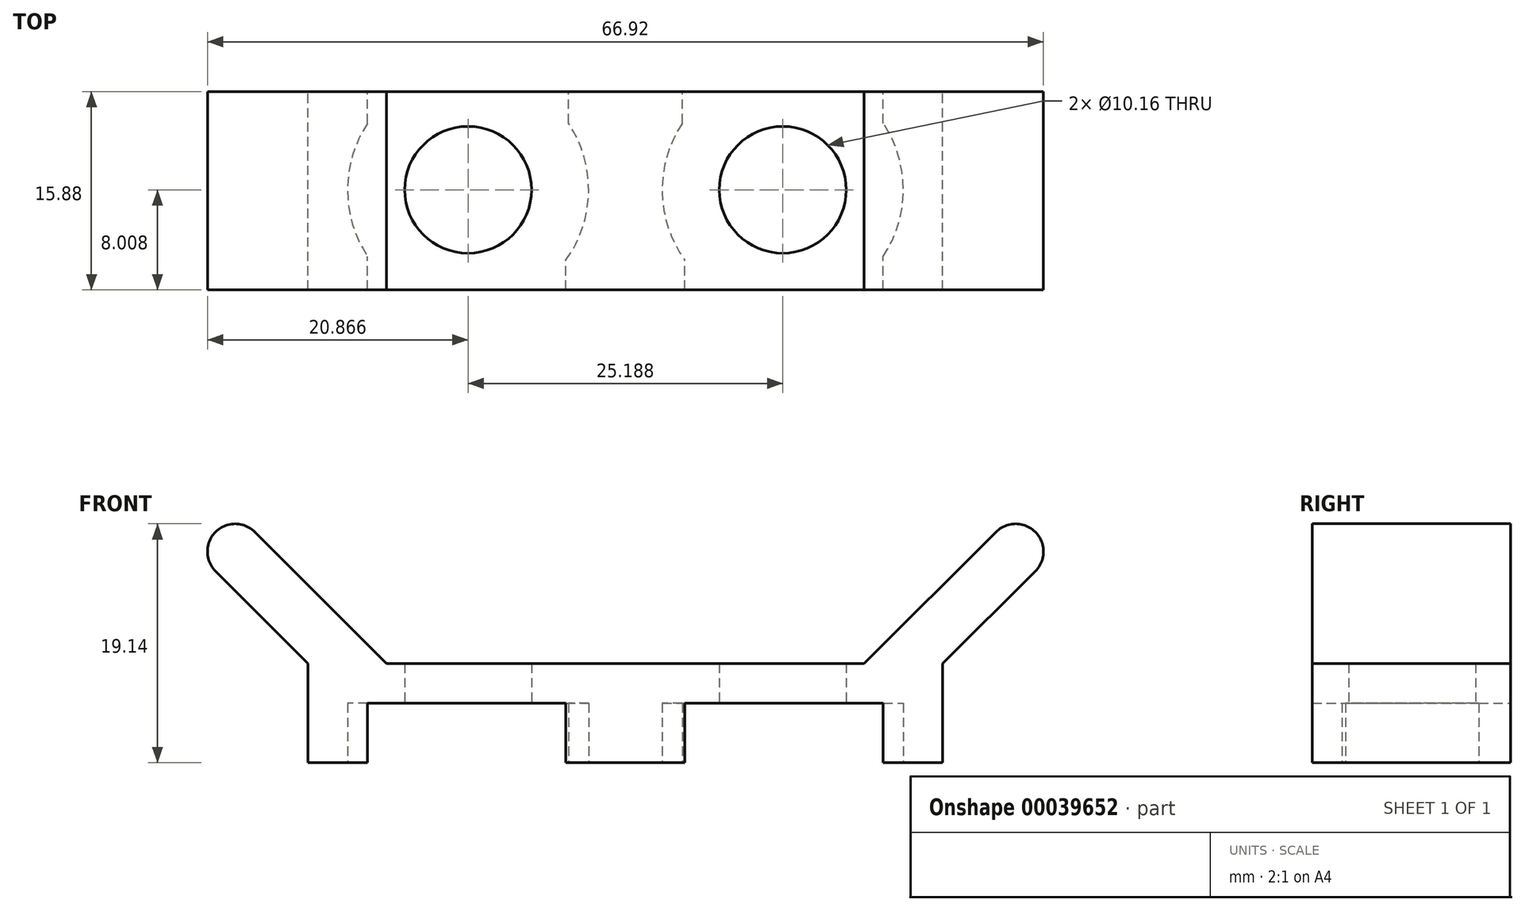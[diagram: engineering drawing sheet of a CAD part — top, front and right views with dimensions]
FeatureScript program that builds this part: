
annotation { "Feature Type Name" : "Feature", "Feature Type Description" : "" }
export const myFeature = defineFeature(function(context is Context, id is Id, definition is map)
    precondition{}
    {
        {
            var Q0;
            Q0=qCreatedBy(makeId("Top.planeOp"),FACE);
            var sketch = newSketch(context, id + "F0", { "sketchPlane" : qUnion([Q0])});
            skLineSegment(sketch, "E0", {"start": v(0, 0) * mm, "end": v(0, 15.88) * mm});
            skLineSegment(sketch, "E1", {"start": v(0, 15.88) * mm, "end": v(25.4, 15.88) * mm});
            skLineSegment(sketch, "E2", {"start": v(25.4, 15.88) * mm, "end": v(25.4, 0) * mm});
            skLineSegment(sketch, "E3", {"start": v(25.4, 0) * mm, "end": v(0, 0) * mm});
            skLineSegment(sketch, "E4", {"start": v(0, 15.88) * mm, "end": v(3.18, 15.88) * mm});
            skPoint(sketch, "E5.endSnap0", {"position": v(3.28, 8) * mm});
            skArc(sketch, "E6", {"start": v(7.21, 15.87) * mm, "mid": v(3.15, 7.88) * mm, "end": v(7.42, 0) * mm});
            skPoint(sketch, "E7.startSnap0", {"position": v(25.4, 7.94) * mm});
            skArc(sketch, "E8.trimOffspring", {"start": v(18.2, 0) * mm, "mid": v(22.46, 7.88) * mm, "end": v(18.4, 15.88) * mm});
            skLineSegment(sketch, "E9", {"start": v(0, 0) * mm, "end": v(4.76, 0) * mm});
            skLineSegment(sketch, "E10", {"start": v(4.76, 0) * mm, "end": v(4.76, 2.67) * mm});
            skLineSegment(sketch, "E11", {"start": v(4.76, 13.34) * mm, "end": v(4.76, 15.88) * mm});
            skLineSegment(sketch, "E12", {"start": v(25.4, 0) * mm, "end": v(20.64, 0) * mm});
            skLineSegment(sketch, "E13", {"start": v(20.64, 0) * mm, "end": v(20.64, 2.37) * mm});
            skLineSegment(sketch, "E14", {"start": v(20.85, 13.34) * mm, "end": v(20.85, 15.88) * mm});
            skLineSegment(sketch, "E15.MirrorCS", {"start": v(50.8, 15.88) * mm, "end": v(25.4, 15.88) * mm});
            skLineSegment(sketch, "E16.MirrorCS", {"start": v(25.4, 0) * mm, "end": v(30.16, 0) * mm});
            skLineSegment(sketch, "E17.MirrorCS", {"start": v(30.16, 0) * mm, "end": v(30.16, 2.37) * mm});
            skLineSegment(sketch, "E18.MirrorCS", {"start": v(29.95, 13.34) * mm, "end": v(29.95, 15.88) * mm});
            skArc(sketch, "E19.MirrorCS", {"start": v(32.6, 0) * mm, "mid": v(28.34, 7.88) * mm, "end": v(32.4, 15.88) * mm});
            skLineSegment(sketch, "E20.MirrorCS", {"start": v(25.4, 0) * mm, "end": v(50.8, 0) * mm});
            skLineSegment(sketch, "E21.MirrorCS", {"start": v(50.8, 0) * mm, "end": v(50.8, 15.88) * mm});
            skArc(sketch, "E22.MirrorCS", {"start": v(43.59, 15.88) * mm, "mid": v(47.65, 7.88) * mm, "end": v(43.38, 0) * mm});
            skLineSegment(sketch, "E23.MirrorCS", {"start": v(46.04, 13.34) * mm, "end": v(46.04, 15.88) * mm});
            skLineSegment(sketch, "E24.MirrorCS", {"start": v(46.04, 0) * mm, "end": v(46.04, 2.67) * mm});
            skSolve(sketch);
        }
        {
            var Q0;
            {var subQ4=sQuery(id+"F0.wireOp",EDGE,"E0");Q0=makeQuery(id+"F0.imprint","IMPRINT",FACE,{"disambiguationData":[TD([[makeQuery(id+"F0.imprint","IMPRINT",EDGE,{"derivedFrom":subQ4}),-1.0]])]});}
            var Q1;
            {var subQ0=sQuery(id+"F0.wireOp",EDGE,"E2");Q1=makeQuery(id+"F0.imprint","IMPRINT",FACE,{"disambiguationData":[TD([[makeQuery(id+"F0.imprint","IMPRINT",EDGE,{"derivedFrom":subQ0}),-1.0]])]});}
            var Q2;
            {var subQ2=sQuery(id+"F0.wireOp",EDGE,"E2");Q2=makeQuery(id+"F0.imprint","IMPRINT",FACE,{"disambiguationData":[TD([[makeQuery(id+"F0.imprint","IMPRINT",EDGE,{"derivedFrom":subQ2}),1.0]])]});}
            var Q3;
            {var subQ3=sQuery(id+"F0.wireOp",EDGE,"E21.MirrorCS");Q3=makeQuery(id+"F0.imprint","IMPRINT",FACE,{"disambiguationData":[TD([[makeQuery(id+"F0.imprint","IMPRINT",EDGE,{"derivedFrom":subQ3}),1.0]])]});}
            extrude(context, id + "F1", {"entities" : qUnion([Q0, Q1, Q2, Q3]), "depth" : 4.76 * mm});
        }
        {
            var Q0;
            Q0=makeQuery(id+"F1.opExtrude","CAP_FACE",FACE,{"disambiguationData":[OSD([sQuery(id+"F0.wireOp",EDGE,"E0"),sQuery(id+"F0.wireOp",EDGE,"E1"),sQuery(id+"F0.wireOp",EDGE,"E4"),sQuery(id+"F0.wireOp",EDGE,"E6"),sQuery(id+"F0.wireOp",EDGE,"E9"),sQuery(id+"F0.wireOp",EDGE,"E10"),sQuery(id+"F0.wireOp",EDGE,"E11")])],"isStart":false});
            var sketch = newSketch(context, id + "F2", { "sketchPlane" : qUnion([Q0])});
            skPoint(sketch, "E25.0", {"position": v(0, 15.88) * mm});
            skPoint(sketch, "E26.0", {"position": v(4.76, 15.88) * mm});
            skPoint(sketch, "E27.0", {"position": v(20.64, 0) * mm});
            skPoint(sketch, "E28.0", {"position": v(0, 0) * mm});
            skLineSegment(sketch, "E29", {"start": v(0, 15.88) * mm, "end": v(4.76, 15.88) * mm});
            skLineSegment(sketch, "E30", {"start": v(20.64, 0) * mm, "end": v(0, 0) * mm});
            skLineSegment(sketch, "E31", {"start": v(0, 15.88) * mm, "end": v(0, 0) * mm});
            skCircle(sketch, "E32", {"center": v(12.8, 8) * mm, "radius": 5.08 * mm});
            skLineSegment(sketch, "E33", {"start": v(20.64, 0) * mm, "end": v(25.4, 0) * mm});
            skLineSegment(sketch, "E34", {"start": v(25.4, 0) * mm, "end": v(25.4, 2.23) * mm});
            skLineSegment(sketch, "E35.MirrorCS", {"start": v(30.16, 0) * mm, "end": v(25.4, 0) * mm});
            skLineSegment(sketch, "E36.MirrorCS", {"start": v(30.16, 0) * mm, "end": v(50.8, 0) * mm});
            skLineSegment(sketch, "E37.MirrorCS", {"start": v(50.8, 15.88) * mm, "end": v(50.8, 0) * mm});
            skLineSegment(sketch, "E38.MirrorCS", {"start": v(50.8, 15.88) * mm, "end": v(46.04, 15.88) * mm});
            skCircle(sketch, "E39.MirrorC", {"center": v(38, 8) * mm, "radius": 5.08 * mm});
            skLineSegment(sketch, "E40", {"start": v(4.76, 15.88) * mm, "end": v(25.4, 15.88) * mm});
            skLineSegment(sketch, "E41", {"start": v(25.4, 15.88) * mm, "end": v(25.4, 0) * mm});
            skLineSegment(sketch, "E42", {"start": v(25.4, 15.88) * mm, "end": v(46.04, 15.88) * mm});
            skSolve(sketch);
        }
        {
            var Q0;
            Q0=makeQuery(id+"F2.imprint","IMPRINT",FACE,{"disambiguationData":[TD([[makeQuery(id+"F2.imprint","IMPRINT",EDGE,{"derivedFrom":sQuery(id+"F2.wireOp",EDGE,"E32")}),-1.0]])]});
            var Q1;
            {var subQ0=sQuery(id+"F2.wireOp",EDGE,"E35.MirrorCS");Q1=makeQuery(id+"F2.imprint","IMPRINT",FACE,{"disambiguationData":[TD([[makeQuery(id+"F2.imprint","IMPRINT",EDGE,{"derivedFrom":subQ0}),-1.0]])]});}
            var Q2;
            Q2=makeQuery(id+"F2.imprint","IMPRINT",FACE,{"disambiguationData":[TD([[makeQuery(id+"F2.imprint","IMPRINT",EDGE,{"derivedFrom":sQuery(id+"F2.wireOp",EDGE,"E29")}),-1.0]])]});
            extrude(context, id + "F3", {"entities" : qUnion([Q0, Q1, Q2]), "depth" : 3.17 * mm});
        }
        {
            var Q0;
            Q0=makeQuery(id+"F1.opExtrude","SWEPT_BODY",BODY,{"disambiguationData":[OSD([sQuery(id+"F0.wireOp",EDGE,"E0"),sQuery(id+"F0.wireOp",EDGE,"E1"),sQuery(id+"F0.wireOp",EDGE,"E4"),sQuery(id+"F0.wireOp",EDGE,"E6"),sQuery(id+"F0.wireOp",EDGE,"E9"),sQuery(id+"F0.wireOp",EDGE,"E10"),sQuery(id+"F0.wireOp",EDGE,"E11")])]});
            var Q1;
            Q1=makeQuery(id+"F3.opExtrude","SWEPT_BODY",BODY,{"disambiguationData":[OSD([sQuery(id+"F2.wireOp",EDGE,"E29"),sQuery(id+"F2.wireOp",EDGE,"E30"),sQuery(id+"F2.wireOp",EDGE,"E31"),sQuery(id+"F2.wireOp",EDGE,"E32"),sQuery(id+"F2.wireOp",EDGE,"E33"),sQuery(id+"F2.wireOp",EDGE,"E35.MirrorCS"),sQuery(id+"F2.wireOp",EDGE,"E36.MirrorCS"),sQuery(id+"F2.wireOp",EDGE,"E37.MirrorCS"),sQuery(id+"F2.wireOp",EDGE,"E38.MirrorCS"),sQuery(id+"F2.wireOp",EDGE,"E39.MirrorC"),sQuery(id+"F2.wireOp",EDGE,"E40"),sQuery(id+"F2.wireOp",EDGE,"E42")])]});
            var Q2;
            Q2=makeQuery(id+"F1.opExtrude","SWEPT_BODY",BODY,{"disambiguationData":[OSD([sQuery(id+"F0.wireOp",EDGE,"E1"),sQuery(id+"F0.wireOp",EDGE,"E8.trimOffspring"),sQuery(id+"F0.wireOp",EDGE,"E12"),sQuery(id+"F0.wireOp",EDGE,"E13"),sQuery(id+"F0.wireOp",EDGE,"E14"),sQuery(id+"F0.wireOp",EDGE,"E15.MirrorCS"),sQuery(id+"F0.wireOp",EDGE,"E17.MirrorCS"),sQuery(id+"F0.wireOp",EDGE,"E18.MirrorCS"),sQuery(id+"F0.wireOp",EDGE,"E19.MirrorCS"),sQuery(id+"F0.wireOp",EDGE,"E20.MirrorCS")])]});
            var Q3;
            Q3=makeQuery(id+"F1.opExtrude","SWEPT_BODY",BODY,{"disambiguationData":[OSD([sQuery(id+"F0.wireOp",EDGE,"E15.MirrorCS"),sQuery(id+"F0.wireOp",EDGE,"E20.MirrorCS"),sQuery(id+"F0.wireOp",EDGE,"E21.MirrorCS"),sQuery(id+"F0.wireOp",EDGE,"E22.MirrorCS"),sQuery(id+"F0.wireOp",EDGE,"E23.MirrorCS"),sQuery(id+"F0.wireOp",EDGE,"E24.MirrorCS")])]});
            booleanBodies(context, id + "F4", {"operationType" : BooleanOperationType.UNION, "tools" : qUnion([Q0, Q1, Q2, Q3])});
        }
        {
            var Q0;
            {var subQ0=sQuery(id+"F0.wireOp",EDGE,"E20.MirrorCS");Q0=makeQuery(id+"F4.opBoolean","MERGE",FACE,{"derivedFrom":[makeQuery(id+"F1.opExtrude","SWEPT_FACE",FACE,{"disambiguationData":[OSD([sQuery(id+"F0.wireOp",EDGE,"E9")])]}),makeQuery(id+"F1.opExtrude","SWEPT_FACE",FACE,{"disambiguationData":[OSD([sQuery(id+"F0.wireOp",EDGE,"E12"),subQ0])]}),makeQuery(id+"F1.opExtrude","SWEPT_FACE",FACE,{"disambiguationData":[OSD([subQ0])]}),makeQuery(id+"F3.opExtrude","SWEPT_FACE",FACE,{"disambiguationData":[OSD([sQuery(id+"F2.wireOp",EDGE,"E30"),sQuery(id+"F2.wireOp",EDGE,"E33"),sQuery(id+"F2.wireOp",EDGE,"E35.MirrorCS"),sQuery(id+"F2.wireOp",EDGE,"E36.MirrorCS")])]})]});}
            var sketch = newSketch(context, id + "F5", { "sketchPlane" : qUnion([Q0])});
            skLineSegment(sketch, "E43", {"start": v(0, 7.94) * mm, "end": v(-8.98, 16.92) * mm});
            skLineSegment(sketch, "E44", {"start": v(-8.98, 16.92) * mm, "end": v(-5.84, 20.06) * mm});
            skLineSegment(sketch, "E45", {"start": v(-5.84, 20.06) * mm, "end": v(6.29, 7.94) * mm});
            skLineSegment(sketch, "E46", {"start": v(0, 7.94) * mm, "end": v(50.8, 7.94) * mm});
            skLineSegment(sketch, "E47", {"start": v(25.4, 7.94) * mm, "end": v(25.4, 13.63) * mm});
            skLineSegment(sketch, "E48.MirrorCS", {"start": v(56.64, 20.06) * mm, "end": v(44.51, 7.94) * mm});
            skLineSegment(sketch, "E49.MirrorCS", {"start": v(50.8, 7.94) * mm, "end": v(59.78, 16.92) * mm});
            skLineSegment(sketch, "E50.MirrorCS", {"start": v(59.78, 16.92) * mm, "end": v(56.64, 20.06) * mm});
            skSolve(sketch);
        }
        {
            var Q0;
            Q0 = qSketchRegion(id + "F5", true);
            var Q1;
            {var subQ0=sQuery(id+"F5.wireOp",EDGE,"E43");Q1=makeQuery(id+"F5.imprint","IMPRINT",FACE,{"disambiguationData":[TD([[makeQuery(id+"F5.imprint","IMPRINT",EDGE,{"derivedFrom":subQ0}),-1.0]])]});}
            extrude(context, id + "F6", {"entities" : qUnion([Q0, Q1]), "operationType" : NewBodyOperationType.ADD, "oppositeDirection" : true, "depth" : 15.88 * mm});
        }
        {
            var Q0;
            Q0=makeQuery(id+"F6.opExtrude","SWEPT_EDGE",EDGE,{"disambiguationData":[OSD([sQuery(id+"F5.wireOp",EDGE,"E43"),sQuery(id+"F5.wireOp",EDGE,"E44")])]});
            var Q1;
            Q1=makeQuery(id+"F6.opExtrude","SWEPT_EDGE",EDGE,{"disambiguationData":[OSD([sQuery(id+"F5.wireOp",EDGE,"E44"),sQuery(id+"F5.wireOp",EDGE,"E45")])]});
            var Q2;
            Q2=makeQuery(id+"F6.opExtrude","SWEPT_EDGE",EDGE,{"disambiguationData":[OSD([sQuery(id+"F5.wireOp",EDGE,"E48.MirrorCS"),sQuery(id+"F5.wireOp",EDGE,"E50.MirrorCS")])]});
            var Q3;
            Q3=makeQuery(id+"F6.opExtrude","SWEPT_EDGE",EDGE,{"disambiguationData":[OSD([sQuery(id+"F5.wireOp",EDGE,"E49.MirrorCS"),sQuery(id+"F5.wireOp",EDGE,"E50.MirrorCS")])]});
            fillet(context, id + "F7", {"entities" : qUnion([Q0, Q1, Q2, Q3]), "radius" : 2.22 * mm, "tangentPropagation" : true, "allowEdgeOverflow" : false});
        }
    });
